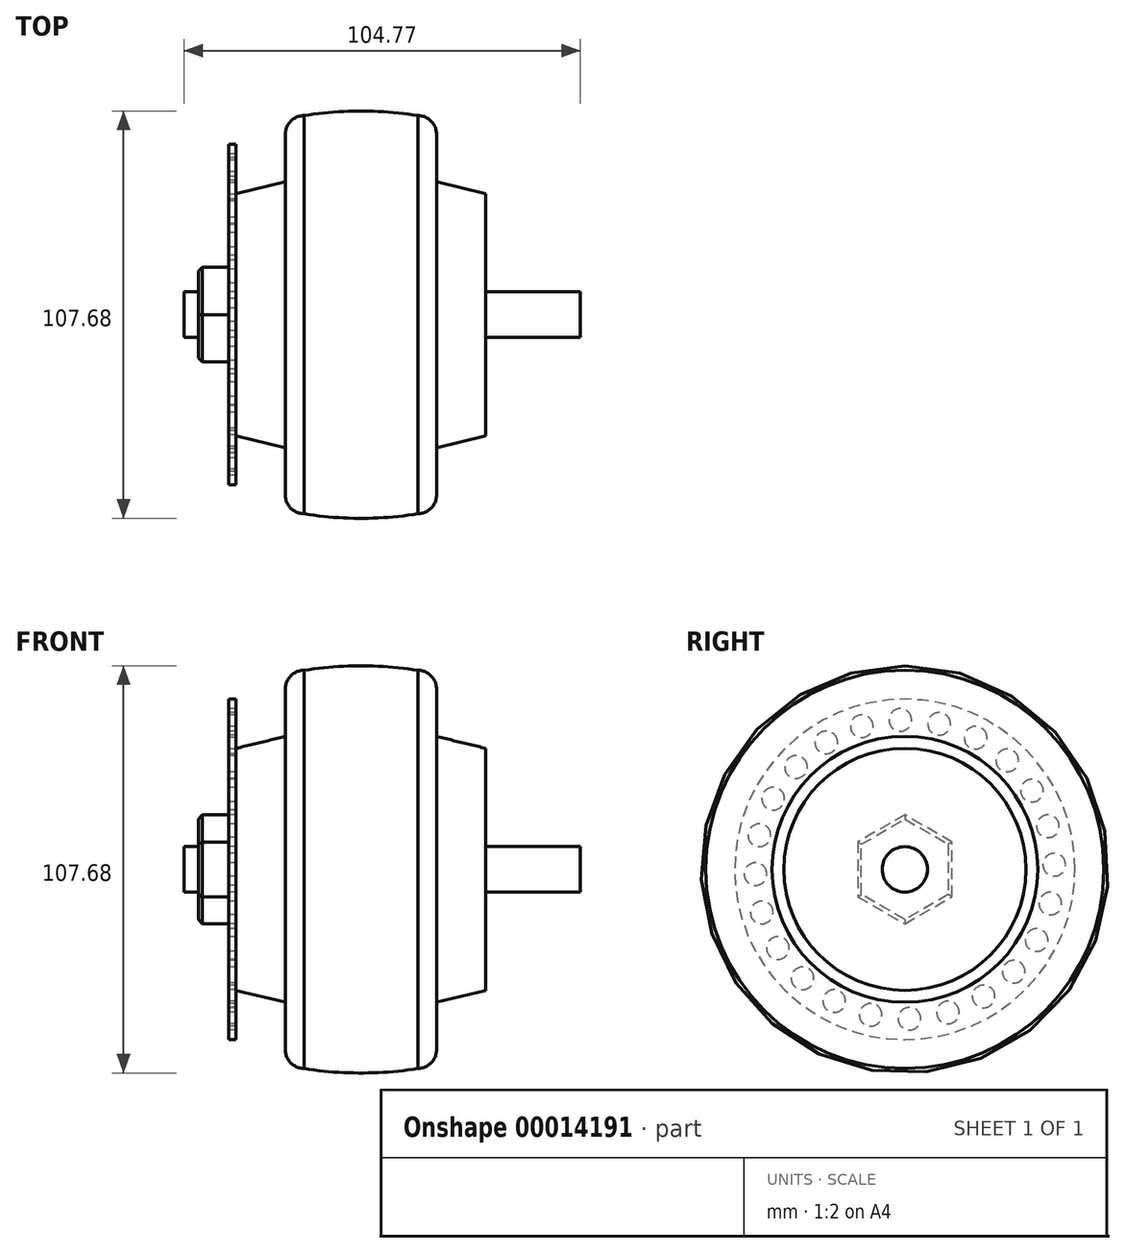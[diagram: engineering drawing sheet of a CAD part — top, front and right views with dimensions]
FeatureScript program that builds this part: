
annotation { "Feature Type Name" : "Feature", "Feature Type Description" : "" }
export const myFeature = defineFeature(function(context is Context, id is Id, definition is map)
    precondition{}
    {
        {
            var Q0;
            Q0=qCreatedBy(makeId("Top.planeOp"),FACE);
            var sketch = newSketch(context, id + "F0", { "sketchPlane" : qUnion([Q0])});
            skLineSegment(sketch, "E0.left", {"start": v(-20, 35.16) * mm, "end": v(-20, 47.66) * mm});
            skLineSegment(sketch, "E0.right", {"start": v(20, 35.16) * mm, "end": v(20, 47.66) * mm});
            skLineSegment(sketch, "E1.right", {"start": v(-33, 0) * mm, "end": v(-33, 32) * mm});
            skLineSegment(sketch, "E2.MirrorCS", {"start": v(33, 0) * mm, "end": v(33, 32) * mm});
            skLineSegment(sketch, "E3", {"start": v(-20, 35.16) * mm, "end": v(-33, 32) * mm});
            skLineSegment(sketch, "E4.MirrorCS", {"start": v(20, 35.16) * mm, "end": v(33, 32) * mm});
            skPoint(sketch, "E5.MirrorCS.end.orphan", {"position": v(29.15, 0) * mm});
            skArc(sketch, "E6.filletArc", {"start": v(-15.04, 52.66) * mm, "mid": v(-18.55, 51.18) * mm, "end": v(-20, 47.66) * mm});
            skArc(sketch, "E7.filletArc", {"start": v(20, 47.66) * mm, "mid": v(18.55, 51.18) * mm, "end": v(15.04, 52.66) * mm});
            skLineSegment(sketch, "E8", {"start": v(-33, 0) * mm, "end": v(33, 0) * mm});
            skArc(sketch, "E9", {"start": v(15.04, 52.66) * mm, "mid": v(0, 53.84) * mm, "end": v(-15.04, 52.66) * mm});
            skSolve(sketch);
        }
        {
            var Q0;
            Q0=qSketchRegion(id+"F0",true);
            var Q1;
            Q1=sQuery(id+"F0.wireOp",EDGE,"E8");
            revolve(context, id + "F1", {"entities" : qUnion([Q0]), "axis" : qUnion([Q1]), "revolveType" : RevolveType.FULL});
        }
        {
            var Q0;
            Q0=makeQuery(id+"F1.opRevolve","SWEPT_FACE",FACE,{"disambiguationData":[OSD([sQuery(id+"F0.wireOp",EDGE,"E2.MirrorCS")])]});
            var sketch = newSketch(context, id + "F2", { "sketchPlane" : qUnion([Q0])});
            skCircle(sketch, "E10", {"center": v(0, 0) * mm, "radius": 6 * mm});
            skSolve(sketch);
        }
        {
            var Q0;
            Q0=qSketchRegion(id+"F2",true);
            extrude(context, id + "F3", {"entities" : qUnion([Q0]), "operationType" : NewBodyOperationType.ADD, "depth" : 25 * mm, "hasSecondDirection" : true, "secondDirectionOppositeDirection" : true, "secondDirectionDepth" : 79.77 * mm});
        }
        {
            var Q0;
            Q0=makeQuery(id+"F1.opRevolve","SWEPT_FACE",FACE,{"disambiguationData":[OSD([sQuery(id+"F0.wireOp",EDGE,"E1.right")])]});
            var sketch = newSketch(context, id + "F4", { "sketchPlane" : qUnion([Q0])});
            skCircle(sketch, "E11", {"center": v(0, 0) * mm, "radius": 45 * mm});
            skSolve(sketch);
        }
        {
            var Q0;
            Q0=qSketchRegion(id+"F4",true);
            extrude(context, id + "F5", {"entities" : qUnion([Q0]), "operationType" : NewBodyOperationType.ADD, "depth" : 2 * mm});
        }
        {
            var Q0;
            Q0=makeQuery(id+"F5.opExtrude","CAP_FACE",FACE,{"disambiguationData":[OSD([sQuery(id+"F4.wireOp",EDGE,"E11")])],"isStart":false});
            var sketch = newSketch(context, id + "F6", { "sketchPlane" : qUnion([Q0])});
            skCircle(sketch, "E12", {"center": v(-9.04, 38.47) * mm, "radius": 3 * mm});
            skSolve(sketch);
        }
        {
            var Q0;
            Q0=qSketchRegion(id+"F6",true);
            extrude(context, id + "F7", {"entities" : qUnion([Q0]), "operationType" : NewBodyOperationType.REMOVE, "endBound" : BoundingType.UP_TO_NEXT, "oppositeDirection" : true, "depth" : 25 * mm});
        }
        {
            var Q0;
            Q0=makeQuery(id+"F7.boolean.opBoolean","COPY",FACE,{"derivedFrom":makeQuery(id+"F7.opExtrude","SWEPT_FACE",FACE,{"disambiguationData":[OSD([sQuery(id+"F6.wireOp",EDGE,"E12")])]})});
            var Q1;
            {var subQ0=sQuery(id+"F2.wireOp",EDGE,"E10");Q1=makeQuery(id+"F3.boolean.opBoolean","SPLIT",FACE,{"disambiguationData":[TD([makeQuery(id+"F1.opRevolve","SWEPT_FACE",FACE,{"disambiguationData":[OSD([sQuery(id+"F0.wireOp",EDGE,"E1.right")])]})])],"derivedFrom":makeQuery(id+"F3.opExtrude","SWEPT_FACE",FACE,{"disambiguationData":[OSD([subQ0])]})});}
            circularPattern(context, id + "F8", {"faces" : qUnion([Q0]), "axis" : qUnion([Q1]), "angle" : 15 * degree, "instanceCount" : 24, "patternType" : PatternType.FACE});
        }
        {
            var Q0;
            Q0=makeQuery(id+"F5.opExtrude","CAP_FACE",FACE,{"disambiguationData":[OSD([sQuery(id+"F4.wireOp",EDGE,"E11")])],"isStart":false});
            var sketch = newSketch(context, id + "F9", { "sketchPlane" : qUnion([Q0])});
            skCircle(sketch, "E13.cCircle", {"center": v(0, 0) * mm, "radius": 12.5 * mm, "construction": true});
            skLineSegment(sketch, "E13.0", {"start": v(12.5, 7.22) * mm, "end": v(12.5, -7.22) * mm});
            skLineSegment(sketch, "E13.1", {"start": v(12.5, -7.22) * mm, "end": v(0, -14.43) * mm});
            skLineSegment(sketch, "E13.2", {"start": v(0, -14.43) * mm, "end": v(-12.5, -7.22) * mm});
            skLineSegment(sketch, "E13.3", {"start": v(-12.5, -7.22) * mm, "end": v(-12.5, 7.22) * mm});
            skLineSegment(sketch, "E13.4", {"start": v(-12.5, 7.22) * mm, "end": v(0, 14.43) * mm});
            skLineSegment(sketch, "E13.5", {"start": v(0, 14.43) * mm, "end": v(12.5, 7.22) * mm});
            skPoint(sketch, "E13.0.midPoint", {"position": v(12.5, 0) * mm});
            skSolve(sketch);
        }
        {
            var Q0;
            Q0=qSketchRegion(id+"F9",true);
            extrude(context, id + "F10", {"entities" : qUnion([Q0]), "operationType" : NewBodyOperationType.ADD, "depth" : 8 * mm});
        }
        {
            var Q0;
            Q0=makeQuery(id+"F10.opExtrude","CAP_EDGE",EDGE,{"disambiguationData":[OSD([sQuery(id+"F9.wireOp",EDGE,"E13.3")])],"isStart":false});
            var Q1;
            Q1=makeQuery(id+"F10.opExtrude","CAP_EDGE",EDGE,{"disambiguationData":[OSD([sQuery(id+"F9.wireOp",EDGE,"E13.4")])],"isStart":false});
            var Q2;
            Q2=makeQuery(id+"F10.opExtrude","CAP_EDGE",EDGE,{"disambiguationData":[OSD([sQuery(id+"F9.wireOp",EDGE,"E13.5")])],"isStart":false});
            var Q3;
            Q3=makeQuery(id+"F10.opExtrude","CAP_EDGE",EDGE,{"disambiguationData":[OSD([sQuery(id+"F9.wireOp",EDGE,"E13.0")])],"isStart":false});
            var Q4;
            Q4=makeQuery(id+"F10.opExtrude","CAP_EDGE",EDGE,{"disambiguationData":[OSD([sQuery(id+"F9.wireOp",EDGE,"E13.1")])],"isStart":false});
            var Q5;
            Q5=makeQuery(id+"F10.opExtrude","CAP_EDGE",EDGE,{"disambiguationData":[OSD([sQuery(id+"F9.wireOp",EDGE,"E13.2")])],"isStart":false});
            chamfer(context, id + "F11", {"entities" : qUnion([Q0, Q1, Q2, Q3, Q4, Q5]), "width" : 1 * mm, "tangentPropagation" : true});
        }
    });
